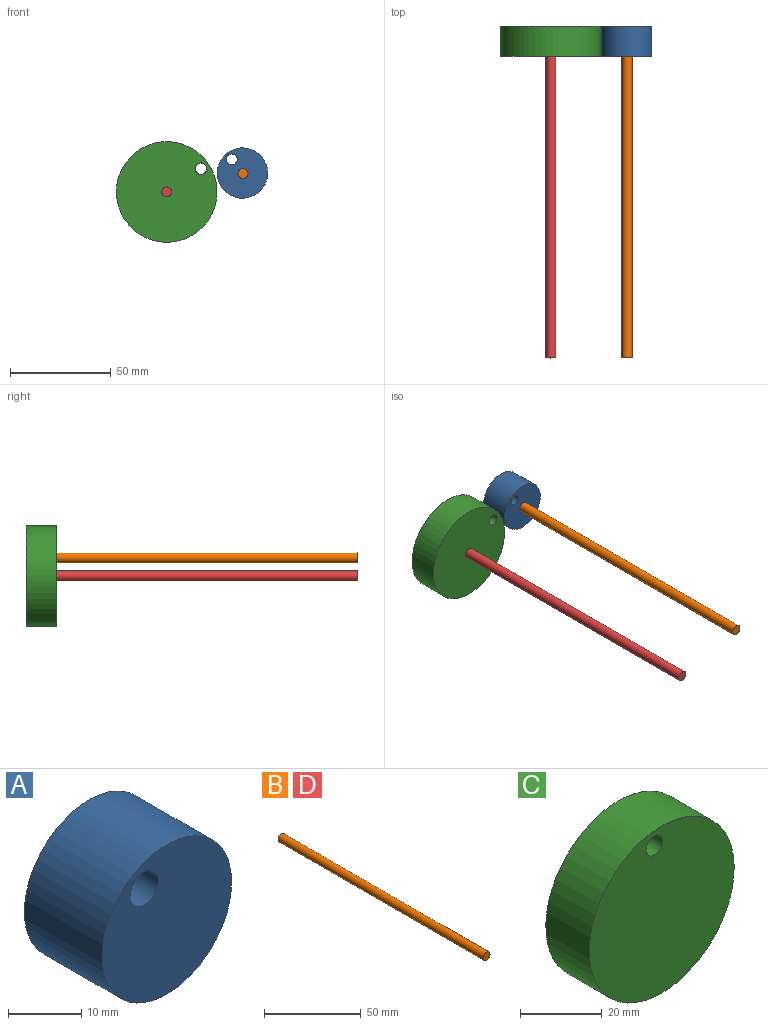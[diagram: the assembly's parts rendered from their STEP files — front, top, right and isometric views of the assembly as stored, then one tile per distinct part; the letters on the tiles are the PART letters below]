
ASSEMBLY  parts=4 mates=3
PART A: 4 faces, bbox 25x15x25 mm
  f0: cylinder r=2.73mm len=15mm, axis (0,1,0), area 257.3mm2, adj f2,f3
  f1: cylinder r=12.5mm len=25mm, axis (0,1,0), area 1178.1mm2, adj f2,f3
  f2: plane 25x25mm, normal (0,-1,0), area 467.5mm2, adj f0,f1
  f3: plane 25x25mm, normal (0,1,0), area 467.5mm2, adj f0,f1
PART B: 3 faces, bbox 5x150x5 mm
  f0: cylinder r=2.5mm len=150mm, axis (0,1,0), area 2356.2mm2, adj f1,f2
  f1: plane 5x5mm, normal (0,-1,0), area 19.6mm2, adj f0
  f2: plane 5x5mm, normal (0,1,0), area 19.6mm2, adj f0
PART C: 4 faces, bbox 50x15x50 mm
  f0: cylinder r=2.85mm len=15mm, axis (0,1,0), area 268.4mm2, adj f2,f3
  f1: cylinder r=25mm len=50mm, axis (0,1,0), area 2356.2mm2, adj f2,f3
  f2: plane 50x50mm, normal (0,-1,0), area 1938mm2, adj f0,f1
  f3: plane 50x50mm, normal (0,1,0), area 1938mm2, adj f0,f1
PART D: same geometry as B
PLACE A rot(axis=(0,-1,0),7.5deg) t=(44.08,63.47,-8.71)mm
PLACE B t=(22.7,48.47,-64.03)mm fixed
PLACE C rot(axis=(0,1,0),62.8deg) t=(34.57,63.47,-45.67)mm
PLACE D rot(axis=(0,-1,0),32.2deg) t=(20.38,48.47,-82.89)mm
MATE parallel D.f0 <-> B.f0  axis (0,1,0) through (19.51,-26.53,-16.4)mm
MATE revolute D.f0 <-> C.f1  axis (0,1,0) through (19.51,48.47,-16.4)mm
MATE revolute A.f2 <-> B.f0  axis (0,-1,0) through (57.43,48.47,-7.33)mm
